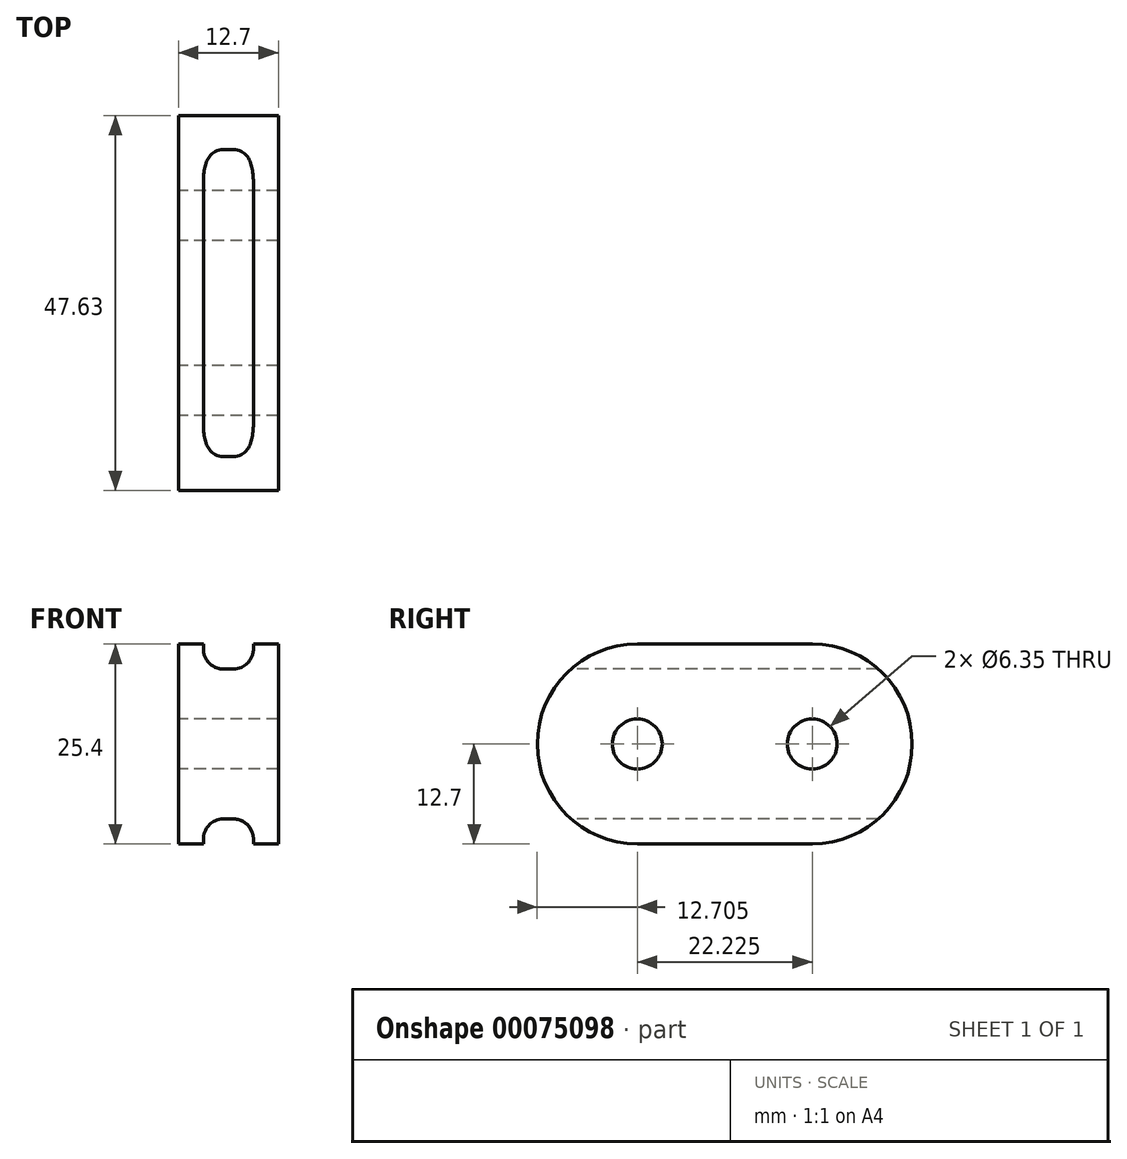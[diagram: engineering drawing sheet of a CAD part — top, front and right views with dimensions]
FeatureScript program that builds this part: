
annotation { "Feature Type Name" : "Feature", "Feature Type Description" : "" }
export const myFeature = defineFeature(function(context is Context, id is Id, definition is map)
    precondition{}
    {
        {
            var Q0;
            Q0=qCreatedBy(makeId("Right.planeOp"),FACE);
            var sketch = newSketch(context, id + "F0", { "sketchPlane" : qUnion([Q0])});
            skCircle(sketch, "E0", {"center": v(0, 0) * mm, "radius": 3.18 * mm});
            skArc(sketch, "E1", {"start": v(0, -12.7) * mm, "mid": v(12.7, 0) * mm, "end": v(0, 12.7) * mm});
            skCircle(sketch, "E2", {"center": v(-22.23, 0) * mm, "radius": 3.18 * mm});
            skArc(sketch, "E3", {"start": v(-22.23, 12.7) * mm, "mid": v(-34.93, 0) * mm, "end": v(-22.22, -12.7) * mm});
            skLineSegment(sketch, "E4", {"start": v(-22.23, 12.7) * mm, "end": v(0, 12.7) * mm});
            skLineSegment(sketch, "E5", {"start": v(-22.23, -12.7) * mm, "end": v(0, -12.7) * mm});
            skSolve(sketch);
        }
        {
            var Q0;
            Q0=makeQuery(id+"F0.imprint","IMPRINT",FACE,{"disambiguationData":[TD([[makeQuery(id+"F0.imprint","IMPRINT",EDGE,{"derivedFrom":sQuery(id+"F0.wireOp",EDGE,"E0")}),-1.0]])]});
            extrude(context, id + "F1", {"entities" : qUnion([Q0]), "endBound" : BoundingType.SYMMETRIC, "depth" : 12.7 * mm});
        }
        {
            var Q0;
            Q0=qCreatedBy(makeId("Front.planeOp"),FACE);
            var sketch = newSketch(context, id + "F2", { "sketchPlane" : qUnion([Q0])});
            skLineSegment(sketch, "E6.rect.bottom", {"start": v(-3.17, 9.53) * mm, "end": v(3.18, 9.53) * mm});
            skLineSegment(sketch, "E6.rect.top", {"start": v(-3.18, 34.24) * mm, "end": v(3.17, 34.24) * mm});
            skLineSegment(sketch, "E6.rect.left", {"start": v(-3.17, 9.53) * mm, "end": v(-3.18, 34.24) * mm});
            skLineSegment(sketch, "E6.rect.right", {"start": v(3.18, 9.53) * mm, "end": v(3.17, 34.24) * mm});
            skPoint(sketch, "E6.rect.middle", {"position": v(0, 21.88) * mm});
            skLineSegment(sketch, "E7.rect.bottom", {"start": v(-3.18, -9.52) * mm, "end": v(3.18, -9.52) * mm});
            skLineSegment(sketch, "E7.rect.top", {"start": v(-3.18, -38.18) * mm, "end": v(3.17, -38.18) * mm});
            skLineSegment(sketch, "E7.rect.left", {"start": v(-3.18, -9.52) * mm, "end": v(-3.18, -38.18) * mm});
            skLineSegment(sketch, "E7.rect.right", {"start": v(3.18, -9.52) * mm, "end": v(3.17, -38.18) * mm});
            skPoint(sketch, "E7.rect.middle", {"position": v(0, -23.85) * mm});
            skSolve(sketch);
        }
        {
            var Q0;
            Q0 = qSketchRegion(id + "F2", true);
            extrude(context, id + "F3", {"entities" : qUnion([Q0]), "operationType" : NewBodyOperationType.REMOVE, "endBound" : BoundingType.SYMMETRIC, "oppositeDirection" : true, "depth" : 101.6 * mm});
        }
        {
            var Q0;
            Q0=makeQuery(id+"F3.boolean.opBoolean","COPY",EDGE,{"derivedFrom":makeQuery(id+"F3.opExtrude","SWEPT_EDGE",EDGE,{"disambiguationData":[OSD([sQuery(id+"F2.wireOp",EDGE,"E6.rect.bottom"),sQuery(id+"F2.wireOp",EDGE,"E6.rect.left")])]})});
            var Q1;
            Q1=makeQuery(id+"F3.boolean.opBoolean","COPY",EDGE,{"derivedFrom":makeQuery(id+"F3.opExtrude","SWEPT_EDGE",EDGE,{"disambiguationData":[OSD([sQuery(id+"F2.wireOp",EDGE,"E6.rect.bottom"),sQuery(id+"F2.wireOp",EDGE,"E6.rect.right")])]})});
            var Q2;
            Q2=makeQuery(id+"F3.boolean.opBoolean","COPY",EDGE,{"derivedFrom":makeQuery(id+"F3.opExtrude","SWEPT_EDGE",EDGE,{"disambiguationData":[OSD([sQuery(id+"F2.wireOp",EDGE,"E7.rect.bottom"),sQuery(id+"F2.wireOp",EDGE,"E7.rect.left")])]})});
            var Q3;
            Q3=makeQuery(id+"F3.boolean.opBoolean","COPY",EDGE,{"derivedFrom":makeQuery(id+"F3.opExtrude","SWEPT_EDGE",EDGE,{"disambiguationData":[OSD([sQuery(id+"F2.wireOp",EDGE,"E7.rect.bottom"),sQuery(id+"F2.wireOp",EDGE,"E7.rect.right")])]})});
            fillet(context, id + "F4", {"entities" : qUnion([Q0, Q1, Q2, Q3]), "radius" : 2.54 * mm, "tangentPropagation" : true, "allowEdgeOverflow" : false});
        }
    });
